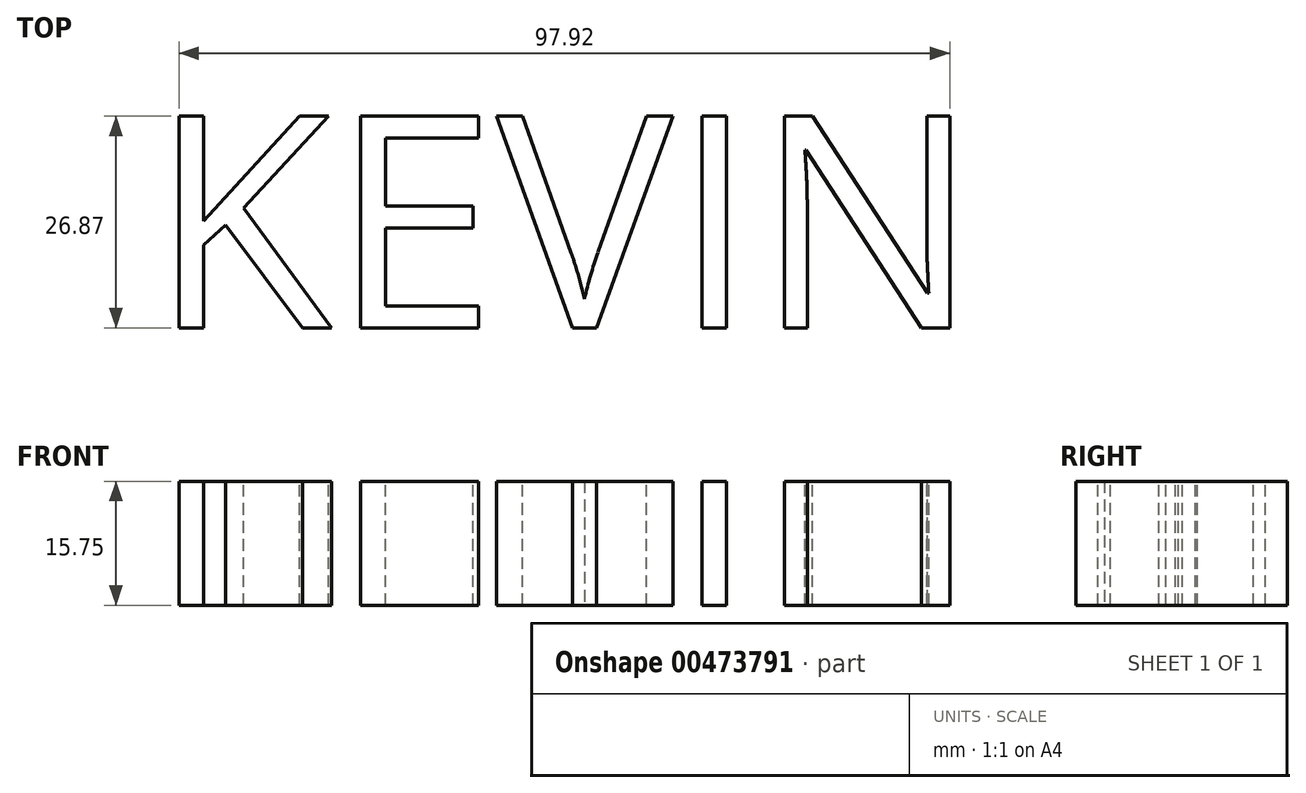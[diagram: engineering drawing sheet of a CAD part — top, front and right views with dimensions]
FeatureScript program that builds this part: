
annotation { "Feature Type Name" : "Feature", "Feature Type Description" : "" }
export const myFeature = defineFeature(function(context is Context, id is Id, definition is map)
    precondition{}
    {
        {
            var Q0;
            Q0=qCreatedBy(makeId("Top.planeOp"),FACE);
            var sketch = newSketch(context, id + "F0", { "sketchPlane" : qUnion([Q0])});
            skText(sketch, "E0", { "text": "KEVIN\n", "fontName": "OpenSans-Regular.ttf"});
            const initialGuessF0  = {"E0": [-0.13363, -0.04817, 1, 0, 0.0271]};
            skSetInitialGuess(sketch, initialGuessF0);
            skSolve(sketch);
        }
        {
            var Q0;
            Q0 = qConstructionFilter(qBodyType(qCreatedBy(id + "F0" ,EDGE), BodyType.WIRE), ConstructionObject.NO);
            extrude(context, id + "F1", {"bodyType" : ToolBodyType.SURFACE, "surfaceEntities" : qUnion([Q0]), "depth" : 15.75 * mm});
        }
    });
